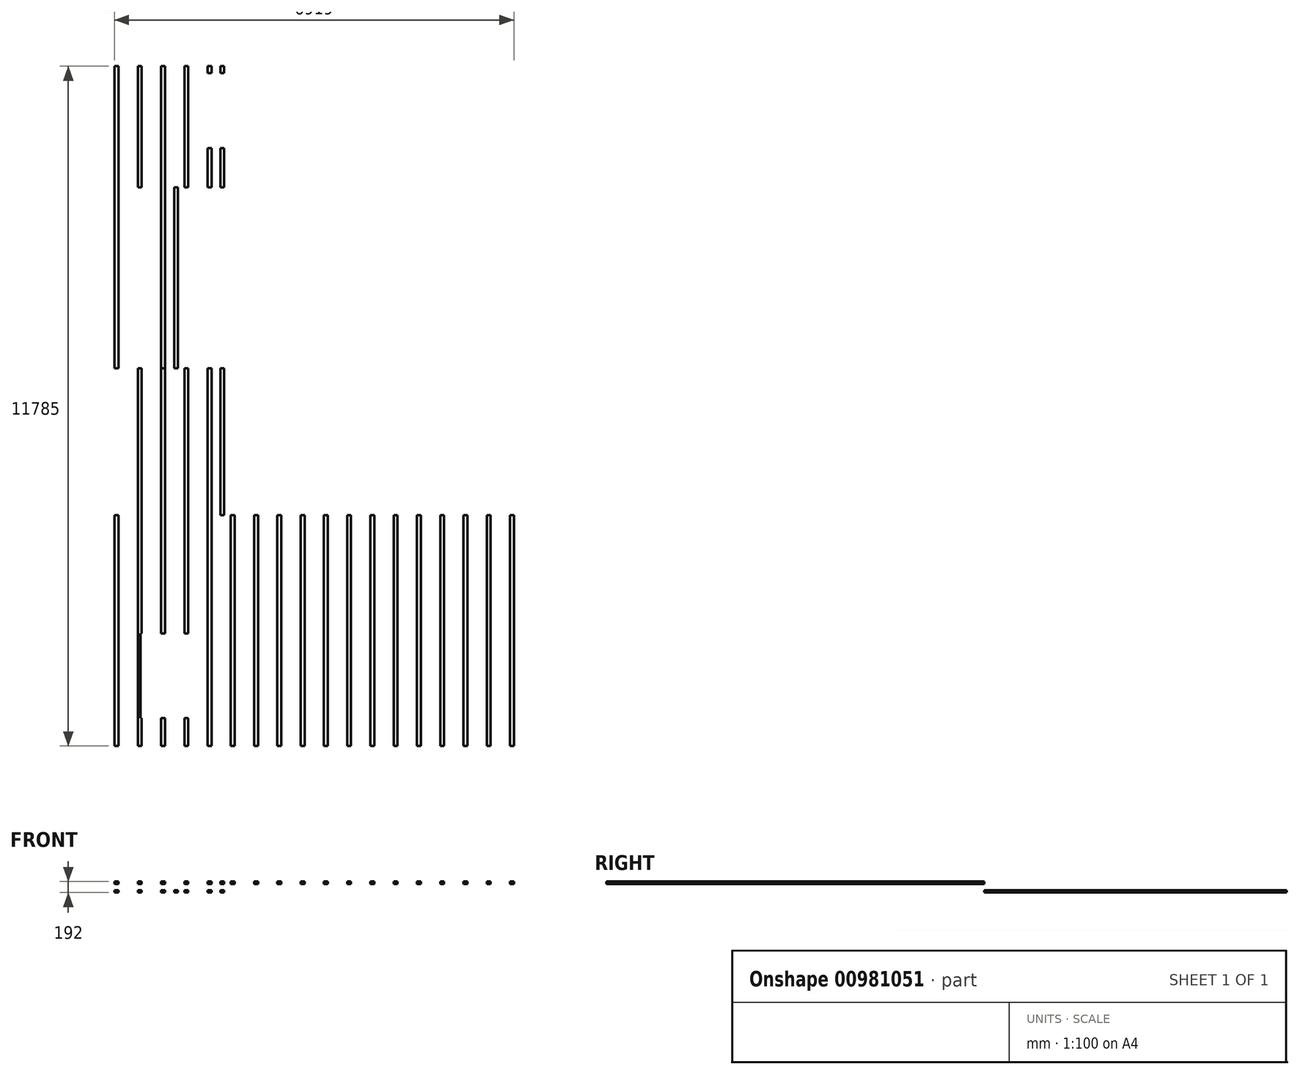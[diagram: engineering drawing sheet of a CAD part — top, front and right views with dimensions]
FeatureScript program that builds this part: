
annotation { "Feature Type Name" : "Feature", "Feature Type Description" : "" }
export const myFeature = defineFeature(function(context is Context, id is Id, definition is map)
    precondition{}
    {
        {
            var Q0;
            Q0=qCreatedBy(makeId("Top.planeOp"),FACE);
            var sketch = newSketch(context, id + "F0", { "sketchPlane" : qUnion([Q0])});
            skLineSegment(sketch, "E0.bottom", {"start": v(25.8, 3170.51) * mm, "end": v(93.8, 3170.51) * mm});
            skLineSegment(sketch, "E0.top", {"start": v(25.8, -829.49) * mm, "end": v(93.8, -829.49) * mm});
            skLineSegment(sketch, "E0.left", {"start": v(25.8, 3170.51) * mm, "end": v(25.8, -829.49) * mm});
            skLineSegment(sketch, "E0.right", {"start": v(93.8, 3170.51) * mm, "end": v(93.8, -829.49) * mm});
            skLineSegment(sketch, "E1.1.0.0", {"start": v(428.8, 3170.51) * mm, "end": v(428.8, -829.49) * mm});
            skLineSegment(sketch, "E1.1.0.1", {"start": v(496.8, 3170.51) * mm, "end": v(496.8, -829.49) * mm});
            skLineSegment(sketch, "E1.1.0.2", {"start": v(428.8, -829.49) * mm, "end": v(496.8, -829.49) * mm});
            skLineSegment(sketch, "E1.1.0.3", {"start": v(428.8, 3170.51) * mm, "end": v(496.8, 3170.51) * mm});
            skLineSegment(sketch, "E1.2.0.0", {"start": v(831.8, 3170.51) * mm, "end": v(831.8, -829.49) * mm});
            skLineSegment(sketch, "E1.2.0.1", {"start": v(899.8, 3170.51) * mm, "end": v(899.8, -829.49) * mm});
            skLineSegment(sketch, "E1.2.0.2", {"start": v(831.8, -829.49) * mm, "end": v(899.8, -829.49) * mm});
            skLineSegment(sketch, "E1.2.0.3", {"start": v(831.8, 3170.51) * mm, "end": v(899.8, 3170.51) * mm});
            skLineSegment(sketch, "E1.3.0.0", {"start": v(1234.8, 3170.51) * mm, "end": v(1234.8, -829.49) * mm});
            skLineSegment(sketch, "E1.3.0.1", {"start": v(1302.8, 3170.51) * mm, "end": v(1302.8, -829.49) * mm});
            skLineSegment(sketch, "E1.3.0.2", {"start": v(1234.8, -829.49) * mm, "end": v(1302.8, -829.49) * mm});
            skLineSegment(sketch, "E1.3.0.3", {"start": v(1234.8, 3170.51) * mm, "end": v(1302.8, 3170.51) * mm});
            skLineSegment(sketch, "E1.4.0.0", {"start": v(1637.8, 3170.51) * mm, "end": v(1637.8, -829.49) * mm});
            skLineSegment(sketch, "E1.4.0.1", {"start": v(1705.8, 3170.51) * mm, "end": v(1705.8, -829.49) * mm});
            skLineSegment(sketch, "E1.4.0.2", {"start": v(1637.8, -829.49) * mm, "end": v(1705.8, -829.49) * mm});
            skLineSegment(sketch, "E1.4.0.3", {"start": v(1637.8, 3170.51) * mm, "end": v(1705.8, 3170.51) * mm});
            skLineSegment(sketch, "E1.5.0.0", {"start": v(2040.8, 3170.51) * mm, "end": v(2040.8, -829.49) * mm});
            skLineSegment(sketch, "E1.5.0.1", {"start": v(2108.8, 3170.51) * mm, "end": v(2108.8, -829.49) * mm});
            skLineSegment(sketch, "E1.5.0.2", {"start": v(2040.8, -829.49) * mm, "end": v(2108.8, -829.49) * mm});
            skLineSegment(sketch, "E1.5.0.3", {"start": v(2040.8, 3170.51) * mm, "end": v(2108.8, 3170.51) * mm});
            skLineSegment(sketch, "E1.6.0.0", {"start": v(2443.8, 3170.51) * mm, "end": v(2443.8, -829.49) * mm});
            skLineSegment(sketch, "E1.6.0.1", {"start": v(2511.8, 3170.51) * mm, "end": v(2511.8, -829.49) * mm});
            skLineSegment(sketch, "E1.6.0.2", {"start": v(2443.8, -829.49) * mm, "end": v(2511.8, -829.49) * mm});
            skLineSegment(sketch, "E1.6.0.3", {"start": v(2443.8, 3170.51) * mm, "end": v(2511.8, 3170.51) * mm});
            skLineSegment(sketch, "E1.7.0.0", {"start": v(2846.8, 3170.51) * mm, "end": v(2846.8, -829.49) * mm});
            skLineSegment(sketch, "E1.7.0.1", {"start": v(2914.8, 3170.51) * mm, "end": v(2914.8, -829.49) * mm});
            skLineSegment(sketch, "E1.7.0.2", {"start": v(2846.8, -829.49) * mm, "end": v(2914.8, -829.49) * mm});
            skLineSegment(sketch, "E1.7.0.3", {"start": v(2846.8, 3170.51) * mm, "end": v(2914.8, 3170.51) * mm});
            skLineSegment(sketch, "E1.8.0.0", {"start": v(3249.8, 3170.51) * mm, "end": v(3249.8, -829.49) * mm});
            skLineSegment(sketch, "E1.8.0.1", {"start": v(3317.8, 3170.51) * mm, "end": v(3317.8, -829.49) * mm});
            skLineSegment(sketch, "E1.8.0.2", {"start": v(3249.8, -829.49) * mm, "end": v(3317.8, -829.49) * mm});
            skLineSegment(sketch, "E1.8.0.3", {"start": v(3249.8, 3170.51) * mm, "end": v(3317.8, 3170.51) * mm});
            skLineSegment(sketch, "E1.9.0.0", {"start": v(3652.8, 3170.51) * mm, "end": v(3652.8, -829.49) * mm});
            skLineSegment(sketch, "E1.9.0.1", {"start": v(3720.8, 3170.51) * mm, "end": v(3720.8, -829.49) * mm});
            skLineSegment(sketch, "E1.9.0.2", {"start": v(3652.8, -829.49) * mm, "end": v(3720.8, -829.49) * mm});
            skLineSegment(sketch, "E1.9.0.3", {"start": v(3652.8, 3170.51) * mm, "end": v(3720.8, 3170.51) * mm});
            skLineSegment(sketch, "E1.10.0.0", {"start": v(4055.8, 3170.51) * mm, "end": v(4055.8, -829.49) * mm});
            skLineSegment(sketch, "E1.10.0.1", {"start": v(4123.8, 3170.51) * mm, "end": v(4123.8, -829.49) * mm});
            skLineSegment(sketch, "E1.10.0.2", {"start": v(4055.8, -829.49) * mm, "end": v(4123.8, -829.49) * mm});
            skLineSegment(sketch, "E1.10.0.3", {"start": v(4055.8, 3170.51) * mm, "end": v(4123.8, 3170.51) * mm});
            skLineSegment(sketch, "E1.11.0.0", {"start": v(4458.8, 3170.51) * mm, "end": v(4458.8, -829.49) * mm});
            skLineSegment(sketch, "E1.11.0.1", {"start": v(4526.8, 3170.51) * mm, "end": v(4526.8, -829.49) * mm});
            skLineSegment(sketch, "E1.11.0.2", {"start": v(4458.8, -829.49) * mm, "end": v(4526.8, -829.49) * mm});
            skLineSegment(sketch, "E1.11.0.3", {"start": v(4458.8, 3170.51) * mm, "end": v(4526.8, 3170.51) * mm});
            skLineSegment(sketch, "E1.12.0.0", {"start": v(4861.8, 3170.51) * mm, "end": v(4861.8, -829.49) * mm});
            skLineSegment(sketch, "E1.12.0.1", {"start": v(4929.8, 3170.51) * mm, "end": v(4929.8, -829.49) * mm});
            skLineSegment(sketch, "E1.12.0.2", {"start": v(4861.8, -829.49) * mm, "end": v(4929.8, -829.49) * mm});
            skLineSegment(sketch, "E1.12.0.3", {"start": v(4861.8, 3170.51) * mm, "end": v(4929.8, 3170.51) * mm});
            skLineSegment(sketch, "E1.13.0.0", {"start": v(5264.8, 3170.51) * mm, "end": v(5264.8, -829.49) * mm});
            skLineSegment(sketch, "E1.13.0.1", {"start": v(5332.8, 3170.51) * mm, "end": v(5332.8, -829.49) * mm});
            skLineSegment(sketch, "E1.13.0.2", {"start": v(5264.8, -829.49) * mm, "end": v(5332.8, -829.49) * mm});
            skLineSegment(sketch, "E1.13.0.3", {"start": v(5264.8, 3170.51) * mm, "end": v(5332.8, 3170.51) * mm});
            skLineSegment(sketch, "E1.14.0.0", {"start": v(5667.8, 3170.51) * mm, "end": v(5667.8, -829.49) * mm});
            skLineSegment(sketch, "E1.14.0.1", {"start": v(5735.8, 3170.51) * mm, "end": v(5735.8, -829.49) * mm});
            skLineSegment(sketch, "E1.14.0.2", {"start": v(5667.8, -829.49) * mm, "end": v(5735.8, -829.49) * mm});
            skLineSegment(sketch, "E1.14.0.3", {"start": v(5667.8, 3170.51) * mm, "end": v(5735.8, 3170.51) * mm});
            skLineSegment(sketch, "E1.direction1", {"start": v(25.8, -829.49) * mm, "end": v(428.8, -829.49) * mm, "construction": true});
            skLineSegment(sketch, "E2.0.15.0", {"start": v(6070.8, 3170.51) * mm, "end": v(6070.8, -829.49) * mm});
            skLineSegment(sketch, "E2.3.15.0", {"start": v(6138.8, 3170.51) * mm, "end": v(6138.8, -829.49) * mm});
            skLineSegment(sketch, "E2.6.15.0", {"start": v(6070.8, -829.49) * mm, "end": v(6138.8, -829.49) * mm});
            skLineSegment(sketch, "E2.9.15.0", {"start": v(6070.8, 3170.51) * mm, "end": v(6138.8, 3170.51) * mm});
            skLineSegment(sketch, "E3.0.16.0", {"start": v(6473.8, 3170.51) * mm, "end": v(6473.8, -829.49) * mm});
            skLineSegment(sketch, "E3.3.16.0", {"start": v(6541.8, 3170.51) * mm, "end": v(6541.8, -829.49) * mm});
            skLineSegment(sketch, "E3.6.16.0", {"start": v(6473.8, -829.49) * mm, "end": v(6541.8, -829.49) * mm});
            skLineSegment(sketch, "E3.9.16.0", {"start": v(6473.8, 3170.51) * mm, "end": v(6541.8, 3170.51) * mm});
            skLineSegment(sketch, "E3.0.17.0", {"start": v(6876.8, 3170.51) * mm, "end": v(6876.8, -829.49) * mm});
            skLineSegment(sketch, "E3.3.17.0", {"start": v(6944.8, 3170.51) * mm, "end": v(6944.8, -829.49) * mm});
            skLineSegment(sketch, "E3.6.17.0", {"start": v(6876.8, -829.49) * mm, "end": v(6944.8, -829.49) * mm});
            skLineSegment(sketch, "E3.9.17.0", {"start": v(6876.8, 3170.51) * mm, "end": v(6944.8, 3170.51) * mm});
            skLineSegment(sketch, "E4.bottom", {"start": v(93.8, 3170.51) * mm, "end": v(25.8, 3170.51) * mm});
            skLineSegment(sketch, "E4.top", {"start": v(93.8, 5716.51) * mm, "end": v(25.8, 5716.51) * mm});
            skLineSegment(sketch, "E4.left", {"start": v(93.8, 3170.51) * mm, "end": v(93.8, 5716.51) * mm});
            skLineSegment(sketch, "E4.right", {"start": v(25.8, 3170.51) * mm, "end": v(25.8, 5716.51) * mm});
            skLineSegment(sketch, "E5.1.0.0", {"start": v(496.8, 3170.51) * mm, "end": v(496.8, 5716.51) * mm});
            skLineSegment(sketch, "E5.1.0.1", {"start": v(428.8, 3170.51) * mm, "end": v(428.8, 5716.51) * mm});
            skLineSegment(sketch, "E5.1.0.2", {"start": v(496.8, 5716.51) * mm, "end": v(428.8, 5716.51) * mm});
            skLineSegment(sketch, "E5.1.0.3", {"start": v(496.8, 3170.51) * mm, "end": v(428.8, 3170.51) * mm});
            skLineSegment(sketch, "E5.2.0.0", {"start": v(899.8, 3170.51) * mm, "end": v(899.8, 5716.51) * mm});
            skLineSegment(sketch, "E5.2.0.1", {"start": v(831.8, 3170.51) * mm, "end": v(831.8, 5716.51) * mm});
            skLineSegment(sketch, "E5.2.0.2", {"start": v(899.8, 5716.51) * mm, "end": v(831.8, 5716.51) * mm});
            skLineSegment(sketch, "E5.2.0.3", {"start": v(899.8, 3170.51) * mm, "end": v(831.8, 3170.51) * mm});
            skLineSegment(sketch, "E5.3.0.0", {"start": v(1302.8, 3170.51) * mm, "end": v(1302.8, 5716.51) * mm});
            skLineSegment(sketch, "E5.3.0.1", {"start": v(1234.8, 3170.51) * mm, "end": v(1234.8, 5716.51) * mm});
            skLineSegment(sketch, "E5.3.0.2", {"start": v(1302.8, 5716.51) * mm, "end": v(1234.8, 5716.51) * mm});
            skLineSegment(sketch, "E5.3.0.3", {"start": v(1302.8, 3170.51) * mm, "end": v(1234.8, 3170.51) * mm});
            skLineSegment(sketch, "E5.4.0.0", {"start": v(1705.8, 3170.51) * mm, "end": v(1705.8, 5716.51) * mm});
            skLineSegment(sketch, "E5.4.0.1", {"start": v(1637.8, 3170.51) * mm, "end": v(1637.8, 5716.51) * mm});
            skLineSegment(sketch, "E5.4.0.2", {"start": v(1705.8, 5716.51) * mm, "end": v(1637.8, 5716.51) * mm});
            skLineSegment(sketch, "E5.4.0.3", {"start": v(1705.8, 3170.51) * mm, "end": v(1637.8, 3170.51) * mm});
            skLineSegment(sketch, "E5.direction1", {"start": v(93.8, 3170.51) * mm, "end": v(496.8, 3170.51) * mm, "construction": true});
            skLineSegment(sketch, "E6.1.0.0", {"start": v(1857.8, 3170.51) * mm, "end": v(1925.8, 3170.51) * mm});
            skLineSegment(sketch, "E6.1.0.1", {"start": v(1925.8, 3170.51) * mm, "end": v(1925.8, 5716.51) * mm});
            skLineSegment(sketch, "E6.1.0.2", {"start": v(1925.8, 5716.51) * mm, "end": v(1857.8, 5716.51) * mm});
            skLineSegment(sketch, "E6.1.0.3", {"start": v(1857.8, 3170.51) * mm, "end": v(1857.8, 5716.51) * mm});
            skLineSegment(sketch, "E6.direction1", {"start": v(1637.8, 3170.51) * mm, "end": v(1857.8, 3170.51) * mm, "construction": true});
            skLineSegment(sketch, "E7.top", {"start": v(93.8, 8855.51) * mm, "end": v(25.8, 8855.51) * mm});
            skLineSegment(sketch, "E7.left", {"start": v(93.8, 5716.51) * mm, "end": v(93.8, 8855.51) * mm});
            skLineSegment(sketch, "E7.right", {"start": v(25.8, 5716.51) * mm, "end": v(25.8, 8855.51) * mm});
            skLineSegment(sketch, "E8.1.0.1", {"start": v(496.8, 5716.51) * mm, "end": v(496.8, 8855.51) * mm});
            skLineSegment(sketch, "E8.1.0.2", {"start": v(428.8, 5716.51) * mm, "end": v(428.8, 8855.51) * mm});
            skLineSegment(sketch, "E8.1.0.3", {"start": v(496.8, 8855.51) * mm, "end": v(428.8, 8855.51) * mm});
            skLineSegment(sketch, "E8.2.0.1", {"start": v(899.8, 5716.51) * mm, "end": v(899.8, 8855.51) * mm});
            skLineSegment(sketch, "E8.2.0.2", {"start": v(831.8, 5716.51) * mm, "end": v(831.8, 8855.51) * mm});
            skLineSegment(sketch, "E8.2.0.3", {"start": v(899.8, 8855.51) * mm, "end": v(831.8, 8855.51) * mm});
            skLineSegment(sketch, "E8.direction1", {"start": v(25.8, 5716.51) * mm, "end": v(428.8, 5716.51) * mm, "construction": true});
            skLineSegment(sketch, "E9.1.0.0", {"start": v(1125.8, 5716.51) * mm, "end": v(1125.8, 8855.51) * mm});
            skLineSegment(sketch, "E9.1.0.1", {"start": v(1057.8, 5716.51) * mm, "end": v(1057.8, 8855.51) * mm});
            skLineSegment(sketch, "E9.1.0.2", {"start": v(1125.8, 8855.51) * mm, "end": v(1057.8, 8855.51) * mm});
            skLineSegment(sketch, "E9.1.0.3", {"start": v(1125.8, 5716.51) * mm, "end": v(1057.8, 5716.51) * mm});
            skLineSegment(sketch, "E9.direction1", {"start": v(831.8, 5716.51) * mm, "end": v(1057.8, 5716.51) * mm, "construction": true});
            skLineSegment(sketch, "E10.top", {"start": v(93.8, 10955.51) * mm, "end": v(25.8, 10955.51) * mm});
            skLineSegment(sketch, "E10.left", {"start": v(93.8, 8855.51) * mm, "end": v(93.8, 10955.51) * mm});
            skLineSegment(sketch, "E10.right", {"start": v(25.8, 8855.51) * mm, "end": v(25.8, 10955.51) * mm});
            skLineSegment(sketch, "E11.bottom", {"start": v(25.8, 10955.51) * mm, "end": v(93.8, 10955.51) * mm});
            skLineSegment(sketch, "E12.1.0.0", {"start": v(496.8, 8855.51) * mm, "end": v(496.8, 10955.51) * mm});
            skLineSegment(sketch, "E12.1.0.1", {"start": v(428.8, 8855.51) * mm, "end": v(428.8, 10955.51) * mm});
            skLineSegment(sketch, "E12.1.0.2", {"start": v(496.8, 10955.51) * mm, "end": v(428.8, 10955.51) * mm});
            skLineSegment(sketch, "E12.2.0.0", {"start": v(899.8, 8855.51) * mm, "end": v(899.8, 10955.51) * mm});
            skLineSegment(sketch, "E12.2.0.1", {"start": v(831.8, 8855.51) * mm, "end": v(831.8, 10955.51) * mm});
            skLineSegment(sketch, "E12.2.0.2", {"start": v(899.8, 10955.51) * mm, "end": v(831.8, 10955.51) * mm});
            skLineSegment(sketch, "E12.3.0.0", {"start": v(1302.8, 8855.51) * mm, "end": v(1302.8, 10955.51) * mm});
            skLineSegment(sketch, "E12.3.0.1", {"start": v(1234.8, 8855.51) * mm, "end": v(1234.8, 10955.51) * mm});
            skLineSegment(sketch, "E12.3.0.2", {"start": v(1302.8, 10955.51) * mm, "end": v(1234.8, 10955.51) * mm});
            skLineSegment(sketch, "E12.3.0.3", {"start": v(1302.8, 8855.51) * mm, "end": v(1234.8, 8855.51) * mm});
            skLineSegment(sketch, "E12.4.0.0", {"start": v(1705.8, 8855.51) * mm, "end": v(1705.8, 10955.51) * mm});
            skLineSegment(sketch, "E12.4.0.1", {"start": v(1637.8, 8855.51) * mm, "end": v(1637.8, 10955.51) * mm});
            skLineSegment(sketch, "E12.4.0.2", {"start": v(1705.8, 10955.51) * mm, "end": v(1637.8, 10955.51) * mm});
            skLineSegment(sketch, "E12.4.0.3", {"start": v(1705.8, 8855.51) * mm, "end": v(1637.8, 8855.51) * mm});
            skLineSegment(sketch, "E12.direction1", {"start": v(25.8, 8855.51) * mm, "end": v(428.8, 8855.51) * mm, "construction": true});
            skLineSegment(sketch, "E13.1.0.0", {"start": v(1925.8, 8855.51) * mm, "end": v(1925.8, 10955.51) * mm});
            skLineSegment(sketch, "E13.1.0.1", {"start": v(1857.8, 8855.51) * mm, "end": v(1857.8, 10955.51) * mm});
            skLineSegment(sketch, "E13.1.0.2", {"start": v(1925.8, 10955.51) * mm, "end": v(1857.8, 10955.51) * mm});
            skLineSegment(sketch, "E13.1.0.3", {"start": v(1925.8, 8855.51) * mm, "end": v(1857.8, 8855.51) * mm});
            skLineSegment(sketch, "E13.direction1", {"start": v(1637.8, 8855.51) * mm, "end": v(1857.8, 8855.51) * mm, "construction": true});
            skLineSegment(sketch, "E14.1.0.3", {"start": v(496.8, 11075.51) * mm, "end": v(428.8, 11075.51) * mm});
            skLineSegment(sketch, "E14.2.0.3", {"start": v(899.8, 11075.51) * mm, "end": v(831.8, 11075.51) * mm});
            skSolve(sketch);
        }
        {
            var Q0;
            Q0=makeQuery(id+"F0.imprint","IMPRINT",FACE,{"disambiguationData":[TD([[makeQuery(id+"F0.imprint","IMPRINT",EDGE,{"derivedFrom":sQuery(id+"F0.wireOp",EDGE,"E0.top")}),1.0]])]});
            var Q1;
            Q1=makeQuery(id+"F0.imprint","IMPRINT",FACE,{"disambiguationData":[TD([[makeQuery(id+"F0.imprint","IMPRINT",EDGE,{"derivedFrom":sQuery(id+"F0.wireOp",EDGE,"E1.1.0.0")}),1.0]])]});
            var Q2;
            Q2=makeQuery(id+"F0.imprint","IMPRINT",FACE,{"disambiguationData":[TD([[makeQuery(id+"F0.imprint","IMPRINT",EDGE,{"derivedFrom":sQuery(id+"F0.wireOp",EDGE,"E1.2.0.0")}),1.0]])]});
            var Q3;
            Q3=makeQuery(id+"F0.imprint","IMPRINT",FACE,{"disambiguationData":[TD([[makeQuery(id+"F0.imprint","IMPRINT",EDGE,{"derivedFrom":sQuery(id+"F0.wireOp",EDGE,"E1.3.0.0")}),1.0]])]});
            var Q4;
            Q4=makeQuery(id+"F0.imprint","IMPRINT",FACE,{"disambiguationData":[TD([[makeQuery(id+"F0.imprint","IMPRINT",EDGE,{"derivedFrom":sQuery(id+"F0.wireOp",EDGE,"E1.6.0.0")}),1.0]])]});
            var Q5;
            Q5=makeQuery(id+"F0.imprint","IMPRINT",FACE,{"disambiguationData":[TD([[makeQuery(id+"F0.imprint","IMPRINT",EDGE,{"derivedFrom":sQuery(id+"F0.wireOp",EDGE,"E1.10.0.0")}),1.0]])]});
            var Q6;
            Q6=makeQuery(id+"F0.imprint","IMPRINT",FACE,{"disambiguationData":[TD([[makeQuery(id+"F0.imprint","IMPRINT",EDGE,{"derivedFrom":sQuery(id+"F0.wireOp",EDGE,"E1.7.0.0")}),1.0]])]});
            var Q7;
            Q7=makeQuery(id+"F0.imprint","IMPRINT",FACE,{"disambiguationData":[TD([[makeQuery(id+"F0.imprint","IMPRINT",EDGE,{"derivedFrom":sQuery(id+"F0.wireOp",EDGE,"E5.4.0.0")}),1.0]])]});
            var Q8;
            Q8=makeQuery(id+"F0.imprint","IMPRINT",FACE,{"disambiguationData":[TD([[makeQuery(id+"F0.imprint","IMPRINT",EDGE,{"derivedFrom":sQuery(id+"F0.wireOp",EDGE,"E1.4.0.0")}),1.0]])]});
            var Q9;
            Q9=makeQuery(id+"F0.imprint","IMPRINT",FACE,{"disambiguationData":[TD([[makeQuery(id+"F0.imprint","IMPRINT",EDGE,{"derivedFrom":sQuery(id+"F0.wireOp",EDGE,"E1.5.0.0")}),1.0]])]});
            var Q10;
            Q10=makeQuery(id+"F0.imprint","IMPRINT",FACE,{"disambiguationData":[TD([[makeQuery(id+"F0.imprint","IMPRINT",EDGE,{"derivedFrom":sQuery(id+"F0.wireOp",EDGE,"E1.13.0.0")}),1.0]])]});
            var Q11;
            Q11=makeQuery(id+"F0.imprint","IMPRINT",FACE,{"disambiguationData":[TD([[makeQuery(id+"F0.imprint","IMPRINT",EDGE,{"derivedFrom":sQuery(id+"F0.wireOp",EDGE,"E1.14.0.0")}),1.0]])]});
            var Q12;
            Q12=makeQuery(id+"F0.imprint","IMPRINT",FACE,{"disambiguationData":[TD([[makeQuery(id+"F0.imprint","IMPRINT",EDGE,{"derivedFrom":sQuery(id+"F0.wireOp",EDGE,"E1.11.0.0")}),1.0]])]});
            var Q13;
            Q13=makeQuery(id+"F0.imprint","IMPRINT",FACE,{"disambiguationData":[TD([[makeQuery(id+"F0.imprint","IMPRINT",EDGE,{"derivedFrom":sQuery(id+"F0.wireOp",EDGE,"E1.8.0.0")}),1.0]])]});
            var Q14;
            Q14=makeQuery(id+"F0.imprint","IMPRINT",FACE,{"disambiguationData":[TD([[makeQuery(id+"F0.imprint","IMPRINT",EDGE,{"derivedFrom":sQuery(id+"F0.wireOp",EDGE,"E1.12.0.0")}),1.0]])]});
            var Q15;
            Q15=makeQuery(id+"F0.imprint","IMPRINT",FACE,{"disambiguationData":[TD([[makeQuery(id+"F0.imprint","IMPRINT",EDGE,{"derivedFrom":sQuery(id+"F0.wireOp",EDGE,"E1.9.0.0")}),1.0]])]});
            var Q16;
            Q16=makeQuery(id+"F0.imprint","IMPRINT",FACE,{"disambiguationData":[TD([[makeQuery(id+"F0.imprint","IMPRINT",EDGE,{"derivedFrom":sQuery(id+"F0.wireOp",EDGE,"E3.0.17.0")}),1.0]])]});
            var Q17;
            Q17=makeQuery(id+"F0.imprint","IMPRINT",FACE,{"disambiguationData":[TD([[makeQuery(id+"F0.imprint","IMPRINT",EDGE,{"derivedFrom":sQuery(id+"F0.wireOp",EDGE,"E5.1.0.0")}),1.0]])]});
            var Q18;
            Q18=makeQuery(id+"F0.imprint","IMPRINT",FACE,{"disambiguationData":[TD([[makeQuery(id+"F0.imprint","IMPRINT",EDGE,{"derivedFrom":sQuery(id+"F0.wireOp",EDGE,"E6.1.0.0")}),1.0]])]});
            var Q19;
            Q19=makeQuery(id+"F0.imprint","IMPRINT",FACE,{"disambiguationData":[TD([[makeQuery(id+"F0.imprint","IMPRINT",EDGE,{"derivedFrom":sQuery(id+"F0.wireOp",EDGE,"E3.0.16.0")}),1.0]])]});
            var Q20;
            Q20=makeQuery(id+"F0.imprint","IMPRINT",FACE,{"disambiguationData":[TD([[makeQuery(id+"F0.imprint","IMPRINT",EDGE,{"derivedFrom":sQuery(id+"F0.wireOp",EDGE,"E5.3.0.0")}),1.0]])]});
            var Q21;
            Q21=makeQuery(id+"F0.imprint","IMPRINT",FACE,{"disambiguationData":[TD([[makeQuery(id+"F0.imprint","IMPRINT",EDGE,{"derivedFrom":sQuery(id+"F0.wireOp",EDGE,"E5.2.0.0")}),1.0]])]});
            var Q22;
            Q22=makeQuery(id+"F0.imprint","IMPRINT",FACE,{"disambiguationData":[TD([[makeQuery(id+"F0.imprint","IMPRINT",EDGE,{"derivedFrom":sQuery(id+"F0.wireOp",EDGE,"E4.bottom")}),-1.0]])]});
            var Q23;
            Q23=makeQuery(id+"F0.imprint","IMPRINT",FACE,{"disambiguationData":[TD([[makeQuery(id+"F0.imprint","IMPRINT",EDGE,{"derivedFrom":sQuery(id+"F0.wireOp",EDGE,"E2.0.15.0")}),1.0]])]});
            extrude(context, id + "F1", {"entities" : qUnion([Q0, Q1, Q2, Q3, Q4, Q5, Q6, Q7, Q8, Q9, Q10, Q11, Q12, Q13, Q14, Q15, Q16, Q17, Q18, Q19, Q20, Q21, Q22, Q23]), "depth" : 42 * mm, "offsetDistance" : 25 * mm});
        }
        {
            var Q0;
            Q0=makeQuery(id+"F0.imprint","IMPRINT",FACE,{"disambiguationData":[TD([[makeQuery(id+"F0.imprint","IMPRINT",EDGE,{"derivedFrom":sQuery(id+"F0.wireOp",EDGE,"E12.4.0.0")}),1.0]])]});
            var Q1;
            Q1=makeQuery(id+"F0.imprint","IMPRINT",FACE,{"disambiguationData":[TD([[makeQuery(id+"F0.imprint","IMPRINT",EDGE,{"derivedFrom":sQuery(id+"F0.wireOp",EDGE,"E12.3.0.0")}),1.0]])]});
            var Q2;
            Q2=makeQuery(id+"F0.imprint","IMPRINT",FACE,{"disambiguationData":[TD([[makeQuery(id+"F0.imprint","IMPRINT",EDGE,{"derivedFrom":sQuery(id+"F0.wireOp",EDGE,"E5.2.0.2")}),-1.0]])]});
            var Q3;
            Q3=makeQuery(id+"F0.imprint","IMPRINT",FACE,{"disambiguationData":[TD([[makeQuery(id+"F0.imprint","IMPRINT",EDGE,{"derivedFrom":sQuery(id+"F0.wireOp",EDGE,"E12.2.0.0")}),1.0]])]});
            var Q4;
            Q4=makeQuery(id+"F0.imprint","IMPRINT",FACE,{"disambiguationData":[TD([[makeQuery(id+"F0.imprint","IMPRINT",EDGE,{"derivedFrom":sQuery(id+"F0.wireOp",EDGE,"E9.1.0.0")}),1.0]])]});
            var Q5;
            Q5=makeQuery(id+"F0.imprint","IMPRINT",FACE,{"disambiguationData":[TD([[makeQuery(id+"F0.imprint","IMPRINT",EDGE,{"derivedFrom":sQuery(id+"F0.wireOp",EDGE,"E12.1.0.0")}),1.0]])]});
            var Q6;
            Q6=makeQuery(id+"F0.imprint","IMPRINT",FACE,{"disambiguationData":[TD([[makeQuery(id+"F0.imprint","IMPRINT",EDGE,{"derivedFrom":sQuery(id+"F0.wireOp",EDGE,"E5.1.0.2")}),-1.0]])]});
            var Q7;
            Q7=makeQuery(id+"F0.imprint","IMPRINT",FACE,{"disambiguationData":[TD([[makeQuery(id+"F0.imprint","IMPRINT",EDGE,{"derivedFrom":sQuery(id+"F0.wireOp",EDGE,"E7.top")}),-1.0]])]});
            var Q8;
            Q8=makeQuery(id+"F0.imprint","IMPRINT",FACE,{"disambiguationData":[TD([[makeQuery(id+"F0.imprint","IMPRINT",EDGE,{"derivedFrom":sQuery(id+"F0.wireOp",EDGE,"E13.1.0.0")}),1.0]])]});
            var Q9;
            Q9=makeQuery(id+"F0.imprint","IMPRINT",FACE,{"disambiguationData":[TD([[makeQuery(id+"F0.imprint","IMPRINT",EDGE,{"derivedFrom":sQuery(id+"F0.wireOp",EDGE,"E4.top")}),-1.0]])]});
            extrude(context, id + "F2", {"entities" : qUnion([Q0, Q1, Q2, Q3, Q4, Q5, Q6, Q7, Q8, Q9]), "oppositeDirection" : true, "depth" : 150 * mm, "offsetDistance" : 25 * mm, "hasSecondDirection" : true, "secondDirectionOppositeDirection" : true, "secondDirectionDepth" : 108 * mm});
        }
        {
            var Q0;
            Q0=makeQuery(id+"F1.opExtrude","CAP_FACE",FACE,{"disambiguationData":[OSD([sQuery(id+"F0.wireOp",EDGE,"E6.1.0.0"),sQuery(id+"F0.wireOp",EDGE,"E6.1.0.1"),sQuery(id+"F0.wireOp",EDGE,"E6.1.0.2"),sQuery(id+"F0.wireOp",EDGE,"E6.1.0.3")])],"isStart":false});
            var sketch = newSketch(context, id + "F3", { "sketchPlane" : qUnion([Q0])});
            skLineSegment(sketch, "E15.bottom", {"start": v(1925.8, 10835.51) * mm, "end": v(1325.8, 10835.51) * mm});
            skLineSegment(sketch, "E15.top", {"start": v(1925.8, 9535.51) * mm, "end": v(1325.8, 9535.51) * mm});
            skLineSegment(sketch, "E15.left", {"start": v(1925.8, 10835.51) * mm, "end": v(1925.8, 9535.51) * mm});
            skLineSegment(sketch, "E15.right", {"start": v(1325.8, 10835.51) * mm, "end": v(1325.8, 9535.51) * mm});
            skLineSegment(sketch, "E16.bottom", {"start": v(478.8, -349.49) * mm, "end": v(1478.8, -349.49) * mm});
            skLineSegment(sketch, "E16.top", {"start": v(478.8, 1120.51) * mm, "end": v(1478.8, 1120.51) * mm});
            skLineSegment(sketch, "E16.left", {"start": v(478.8, -349.49) * mm, "end": v(478.8, 1120.51) * mm});
            skLineSegment(sketch, "E16.right", {"start": v(1478.8, -349.49) * mm, "end": v(1478.8, 1120.51) * mm});
            skSolve(sketch);
        }
        {
            var Q0;
            Q0 = qSketchRegion(id + "F3", true);
            extrude(context, id + "F4", {"entities" : qUnion([Q0]), "operationType" : NewBodyOperationType.REMOVE, "oppositeDirection" : true, "depth" : 1000 * mm, "offsetDistance" : 25 * mm});
        }
    });
